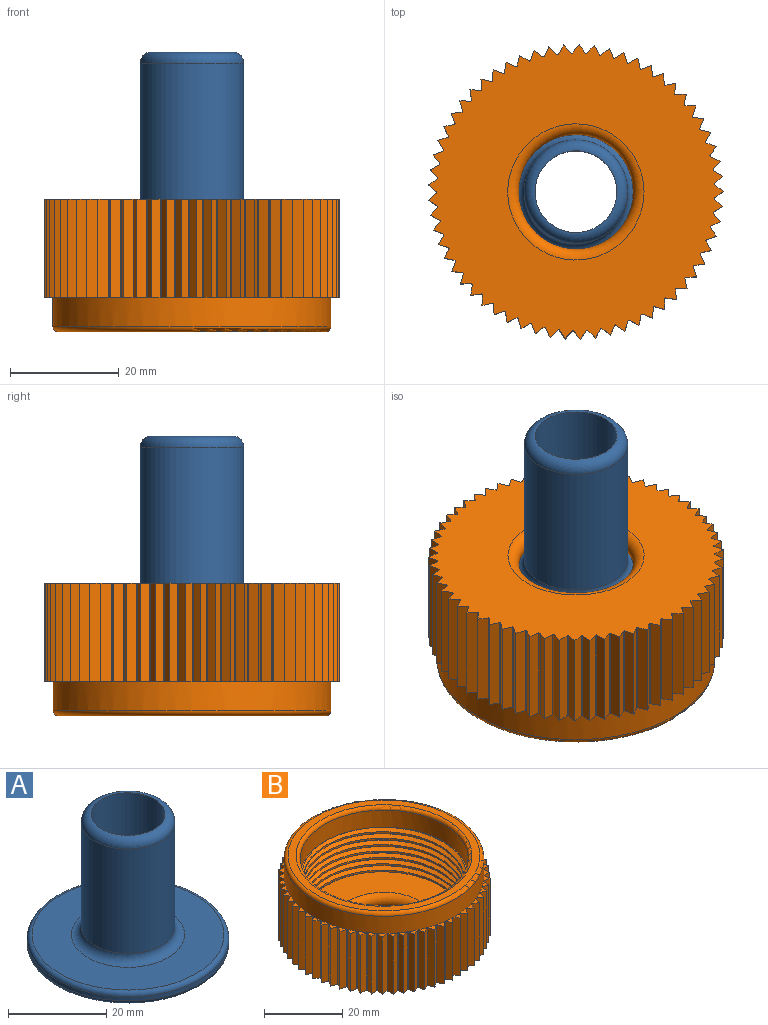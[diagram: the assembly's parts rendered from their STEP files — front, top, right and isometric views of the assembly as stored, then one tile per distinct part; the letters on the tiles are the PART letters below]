
ASSEMBLY  parts=2 mates=1
PART A: 10 faces, bbox 44.4x44.4x33 mm
  f0: cylinder r=20.5mm len=41mm, axis (0,0,-1), area 128.8mm2, adj f7,f8
  f1: cylinder r=7.5mm len=31mm, axis (0,0,-1), area 1460.8mm2, adj f6,f9
  f2: plane 39x39mm, normal (0,0,1), area 779.1mm2, adj f5,f8
  f3: plane 39x39mm, normal (0,0,-1), area 911.1mm2, adj f7,f9
  f4: cylinder r=9.5mm len=26mm, axis (0,0,-1), area 1551.9mm2, adj f5,f6
  f5: torus R=11.5mm, axis (0,0,1), area 201.9mm2, adj f2,f4
  f6: torus R=7.5mm, axis (0,0,1), area 173.2mm2, adj f1,f4
  f7: torus R=19.5mm, axis (0,0,1), area 198.7mm2, adj f0,f3
  f8: torus R=19.5mm, axis (0,0,1), area 198.7mm2, adj f0,f2
  f9: torus R=9.5mm, axis (0,0,1), area 162.4mm2, adj f1,f3
PART B: 197 faces, bbox 56x56x25.1 mm
  f0: plane 2.4x1.71mm, normal (0,0,1), area 1.9mm2, adj f62,f181,f184
  f1: plane 2.37x1.8mm, normal (0,0,1), area 1.9mm2, adj f63,f64,f181
  f2: plane 2.31x1.88mm, normal (0,0,1), area 1.9mm2, adj f65,f66,f181
  f3: plane 2.22x1.94mm, normal (0,0,1), area 1.9mm2, adj f67,f68,f181
  f4: plane 2.11x1.98mm, normal (0,0,1), area 1.9mm2, adj f69,f70,f181
  f5: plane 2x1.98mm, normal (0,0,1), area 1.9mm2, adj f71,f72,f181
  f6: plane 2x1.96mm, normal (0,0,1), area 1.9mm2, adj f73,f74,f181
  f7: plane 1.99x1.97mm, normal (0,0,1), area 1.9mm2, adj f75,f76,f181
  f8: plane 2x1.93mm, normal (0,0,1), area 1.9mm2, adj f77,f78,f181
  f9: plane 2.07x1.99mm, normal (0,0,1), area 1.9mm2, adj f79,f80,f181
  f10: plane 2.18x1.96mm, normal (0,0,1), area 1.9mm2, adj f81,f82,f181
  f11: plane 2.28x1.91mm, normal (0,0,1), area 1.9mm2, adj f83,f84,f181
  f12: plane 2.35x1.83mm, normal (0,0,1), area 1.9mm2, adj f85,f86,f181
  f13: plane 2.4x1.74mm, normal (0,0,1), area 1.9mm2, adj f87,f88,f181
  f14: plane 2.42x1.63mm, normal (0,0,1), area 1.9mm2, adj f89,f90,f181
  f15: plane 2.41x1.68mm, normal (0,0,1), area 1.9mm2, adj f91,f92,f181
  f16: plane 2.38x1.78mm, normal (0,0,1), area 1.9mm2, adj f93,f94,f181
  f17: plane 2.32x1.87mm, normal (0,0,1), area 1.9mm2, adj f95,f96,f181
  f18: plane 2.24x1.93mm, normal (0,0,1), area 1.9mm2, adj f97,f98,f181
  f19: plane 2.14x1.97mm, normal (0,0,1), area 1.9mm2, adj f99,f100,f181
  f20: plane 2.01x2mm, normal (0,0,1), area 1.9mm2, adj f101,f102,f181
  f21: plane 2x1.95mm, normal (0,0,1), area 1.9mm2, adj f103,f104,f181
  f22: plane 1.98x1.98mm, normal (0,0,1), area 1.9mm2, adj f105,f106,f181
  f23: plane 2x1.94mm, normal (0,0,1), area 1.9mm2, adj f107,f108,f181
  f24: plane 2.03x1.99mm, normal (0,0,1), area 1.9mm2, adj f109,f110,f181
  f25: plane 2.16x1.97mm, normal (0,0,1), area 1.9mm2, adj f111,f112,f181
  f26: plane 2.26x1.92mm, normal (0,0,1), area 1.9mm2, adj f113,f114,f181
  f27: plane 2.33x1.85mm, normal (0,0,1), area 1.9mm2, adj f115,f116,f181
  f28: plane 2.39x1.76mm, normal (0,0,1), area 1.9mm2, adj f117,f118,f181
  f29: plane 2.41x1.66mm, normal (0,0,1), area 1.9mm2, adj f119,f120,f181
  f30: plane 2.41x1.65mm, normal (0,0,1), area 1.9mm2, adj f121,f122,f181
  f31: plane 2.39x1.76mm, normal (0,0,1), area 1.9mm2, adj f123,f124,f181
  f32: plane 2.34x1.85mm, normal (0,0,1), area 1.9mm2, adj f125,f126,f181
  f33: plane 2.26x1.92mm, normal (0,0,1), area 1.9mm2, adj f127,f128,f181
  f34: plane 2.17x1.96mm, normal (0,0,1), area 1.9mm2, adj f129,f130,f181
  f35: plane 2.04x1.99mm, normal (0,0,1), area 1.9mm2, adj f131,f132,f181
  f36: plane 2x1.93mm, normal (0,0,1), area 1.9mm2, adj f133,f134,f181
  f37: plane 1.99x1.98mm, normal (0,0,1), area 1.9mm2, adj f135,f136,f181
  f38: plane 2x1.95mm, normal (0,0,1), area 1.9mm2, adj f137,f138,f181
  f39: plane 2x2mm, normal (0,0,1), area 1.9mm2, adj f139,f140,f181
  f40: plane 2.13x1.98mm, normal (0,0,1), area 1.9mm2, adj f141,f142,f181
  f41: plane 2.23x1.93mm, normal (0,0,1), area 1.9mm2, adj f143,f144,f181
  f42: plane 2.32x1.87mm, normal (0,0,1), area 1.9mm2, adj f145,f146,f181
  f43: plane 2.38x1.79mm, normal (0,0,1), area 1.9mm2, adj f147,f148,f181
  f44: plane 2.41x1.69mm, normal (0,0,1), area 1.9mm2, adj f149,f150,f181
  f45: plane 2.42x1.62mm, normal (0,0,1), area 1.9mm2, adj f151,f152,f181
  f46: plane 2.4x1.73mm, normal (0,0,1), area 1.9mm2, adj f153,f154,f181
  f47: plane 2.35x1.83mm, normal (0,0,1), area 1.9mm2, adj f155,f156,f181
  f48: plane 2.29x1.9mm, normal (0,0,1), area 1.9mm2, adj f157,f158,f181
  f49: plane 2.19x1.95mm, normal (0,0,1), area 1.9mm2, adj f159,f160,f181
  f50: plane 2.08x1.99mm, normal (0,0,1), area 1.9mm2, adj f161,f162,f181
  f51: plane 2x1.94mm, normal (0,0,1), area 1.9mm2, adj f163,f164,f181
  f52: plane 1.99x1.97mm, normal (0,0,1), area 1.9mm2, adj f165,f166,f181
  f53: plane 1.99x1.96mm, normal (0,0,1), area 1.9mm2, adj f167,f168,f181
  f54: plane 2x1.96mm, normal (0,0,1), area 1.9mm2, adj f169,f170,f181
  f55: plane 2.1x1.98mm, normal (0,0,1), area 1.9mm2, adj f171,f172,f181
  f56: plane 2.21x1.95mm, normal (0,0,1), area 1.9mm2, adj f173,f174,f181
  f57: plane 2.3x1.89mm, normal (0,0,1), area 1.9mm2, adj f175,f176,f181
  f58: plane 2.36x1.81mm, normal (0,0,1), area 1.9mm2, adj f177,f178,f181
  f59: plane 2.4x1.71mm, normal (0,0,1), area 1.9mm2, adj f179,f180,f181
  f60: plane 2.42x1.6mm, normal (0,0,1), area 1.9mm2, adj f181,f182,f183
  f61: plane 42.7x42.7mm, normal (0,0,1), area 892.4mm2, adj f187,f188,f189,f190,f194
  f62: plane 18x1.71mm, normal (0.52,0.85,0), area 36mm2, adj f0,f181,f184,f185
  f63: plane 18x1.5mm, normal (0.75,-0.66,0), area 36mm2, adj f1,f64,f181,f185
  f64: plane 18x1.8mm, normal (0.43,0.9,0), area 36mm2, adj f1,f63,f181,f185
  f65: plane 18x1.63mm, normal (0.82,-0.58,0), area 36mm2, adj f2,f66,f181,f185
  f66: plane 18x1.88mm, normal (0.34,0.94,0), area 36mm2, adj f2,f65,f181,f185
  f67: plane 18x1.74mm, normal (0.87,-0.49,0), area 36mm2, adj f3,f68,f181,f185
  f68: plane 18x1.94mm, normal (0.24,0.97,0), area 36mm2, adj f3,f67,f181,f185
  f69: plane 18x1.83mm, normal (0.92,-0.4,0), area 36mm2, adj f4,f70,f181,f185
  f70: plane 18x1.98mm, normal (0.14,0.99,0), area 36mm2, adj f4,f69,f181,f185
  f71: plane 18x1.91mm, normal (0.95,-0.3,0), area 36mm2, adj f5,f72,f181,f185
  f72: plane 18x2mm, normal (0.03,1,0), area 36mm2, adj f5,f71,f181,f185
  f73: plane 18x1.96mm, normal (0.98,-0.2,0), area 36mm2, adj f6,f74,f181,f185
  f74: plane 18x2mm, normal (-0.07,1,0), area 36mm2, adj f6,f73,f181,f185
  f75: plane 18x1.99mm, normal (0.99,-0.1,0), area 36mm2, adj f7,f76,f181,f185
  f76: plane 18x1.97mm, normal (-0.17,0.99,0), area 36mm2, adj f7,f75,f181,f185
  f77: plane 18x2mm, normal (1,0,0), area 36mm2, adj f8,f78,f181,f185
  f78: plane 18x1.93mm, normal (-0.27,0.96,0), area 36mm2, adj f8,f77,f181,f185
  f79: plane 18x1.99mm, normal (0.99,0.1,0), area 36mm2, adj f9,f80,f181,f185
  f80: plane 18x1.86mm, normal (-0.37,0.93,0), area 36mm2, adj f9,f79,f181,f185
  f81: plane 18x1.96mm, normal (0.98,0.21,0), area 36mm2, adj f10,f82,f181,f185
  f82: plane 18x1.77mm, normal (-0.46,0.89,0), area 36mm2, adj f10,f81,f181,f185
  f83: plane 18x1.91mm, normal (0.95,0.3,0), area 36mm2, adj f11,f84,f181,f185
  f84: plane 18x1.67mm, normal (-0.55,0.83,0), area 36mm2, adj f11,f83,f181,f185
  f85: plane 18x1.83mm, normal (0.92,0.4,0), area 36mm2, adj f12,f86,f181,f185
  f86: plane 18x1.55mm, normal (-0.63,0.77,0), area 36mm2, adj f12,f85,f181,f185
  f87: plane 18x1.74mm, normal (0.87,0.49,0), area 36mm2, adj f13,f88,f181,f185
  f88: plane 18x1.42mm, normal (-0.71,0.7,0), area 36mm2, adj f13,f87,f181,f185
  f89: plane 18x1.63mm, normal (0.81,0.58,0), area 36mm2, adj f14,f90,f181,f185
  f90: plane 18x1.56mm, normal (-0.78,0.63,0), area 36mm2, adj f14,f89,f181,f185
  f91: plane 18x1.5mm, normal (0.75,0.66,0), area 36mm2, adj f15,f92,f181,f185
  f92: plane 18x1.68mm, normal (-0.84,0.54,0), area 36mm2, adj f15,f91,f181,f185
  f93: plane 18x1.47mm, normal (0.68,0.73,0), area 36mm2, adj f16,f94,f181,f185
  f94: plane 18x1.78mm, normal (-0.89,0.46,0), area 36mm2, adj f16,f93,f181,f185
  f95: plane 18x1.6mm, normal (0.6,0.8,0), area 36mm2, adj f17,f96,f181,f185
  f96: plane 18x1.87mm, normal (-0.93,0.36,0), area 36mm2, adj f17,f95,f181,f185
  f97: plane 18x1.72mm, normal (0.51,0.86,0), area 36mm2, adj f18,f98,f181,f185
  f98: plane 18x1.93mm, normal (-0.96,0.26,0), area 36mm2, adj f18,f97,f181,f185
  f99: plane 18x1.81mm, normal (0.42,0.91,0), area 36mm2, adj f19,f100,f181,f185
  f100: plane 18x1.97mm, normal (-0.99,0.16,0), area 36mm2, adj f19,f99,f181,f185
  f101: plane 18x1.89mm, normal (0.33,0.94,0), area 36mm2, adj f20,f102,f181,f185
  f102: plane 18x2mm, normal (-1,0.06,0), area 36mm2, adj f20,f101,f181,f185
  f103: plane 18x1.95mm, normal (0.23,0.97,0), area 36mm2, adj f21,f104,f181,f185
  f104: plane 18x2mm, normal (-1,-0.04,0), area 36mm2, adj f21,f103,f181,f185
  f105: plane 18x1.98mm, normal (0.13,0.99,0), area 36mm2, adj f22,f106,f181,f185
  f106: plane 18x1.98mm, normal (-0.99,-0.15,0), area 36mm2, adj f22,f105,f181,f185
  f107: plane 18x2mm, normal (0.02,1,0), area 36mm2, adj f23,f108,f181,f185
  f108: plane 18x1.94mm, normal (-0.97,-0.25,0), area 36mm2, adj f23,f107,f181,f185
  f109: plane 18x1.99mm, normal (-0.08,1,0), area 36mm2, adj f24,f110,f181,f185
  f110: plane 18x1.88mm, normal (-0.94,-0.34,0), area 36mm2, adj f24,f109,f181,f185
  f111: plane 18x1.97mm, normal (-0.18,0.98,0), area 36mm2, adj f25,f112,f181,f185
  f112: plane 18x1.8mm, normal (-0.9,-0.44,0), area 36mm2, adj f25,f111,f181,f185
  f113: plane 18x1.92mm, normal (-0.28,0.96,0), area 36mm2, adj f26,f114,f181,f185
  f114: plane 18x1.7mm, normal (-0.85,-0.53,0), area 36mm2, adj f26,f113,f181,f185
  f115: plane 18x1.85mm, normal (-0.38,0.93,0), area 36mm2, adj f27,f116,f181,f185
  f116: plane 18x1.58mm, normal (-0.79,-0.61,0), area 36mm2, adj f27,f115,f181,f185
  f117: plane 18x1.76mm, normal (-0.47,0.88,0), area 36mm2, adj f28,f118,f181,f185
  f118: plane 18x1.44mm, normal (-0.72,-0.69,0), area 36mm2, adj f28,f117,f181,f185
  f119: plane 18x1.66mm, normal (-0.56,0.83,0), area 36mm2, adj f29,f120,f181,f185
  f120: plane 18x1.52mm, normal (-0.65,-0.76,0), area 36mm2, adj f29,f119,f181,f185
  f121: plane 18x1.53mm, normal (-0.64,0.77,0), area 36mm2, adj f30,f122,f181,f185
  f122: plane 18x1.65mm, normal (-0.57,-0.82,0), area 36mm2, adj f30,f121,f181,f185
  f123: plane 18x1.43mm, normal (-0.72,0.7,0), area 36mm2, adj f31,f124,f181,f185
  f124: plane 18x1.76mm, normal (-0.48,-0.88,0), area 36mm2, adj f31,f123,f181,f185
  f125: plane 18x1.57mm, normal (-0.78,0.62,0), area 36mm2, adj f32,f126,f181,f185
  f126: plane 18x1.85mm, normal (-0.39,-0.92,0), area 36mm2, adj f32,f125,f181,f185
  f127: plane 18x1.69mm, normal (-0.84,0.54,0), area 36mm2, adj f33,f128,f181,f185
  f128: plane 18x1.92mm, normal (-0.29,-0.96,0), area 36mm2, adj f33,f127,f181,f185
  f129: plane 18x1.79mm, normal (-0.89,0.45,0), area 36mm2, adj f34,f130,f181,f185
  f130: plane 18x1.96mm, normal (-0.19,-0.98,0), area 36mm2, adj f34,f129,f181,f185
  f131: plane 18x1.87mm, normal (-0.94,0.35,0), area 36mm2, adj f35,f132,f181,f185
  f132: plane 18x1.99mm, normal (-0.09,-1,0), area 36mm2, adj f35,f131,f181,f185
  f133: plane 18x1.93mm, normal (-0.97,0.25,0), area 36mm2, adj f36,f134,f181,f185
  f134: plane 18x2mm, normal (0.02,-1,0), area 36mm2, adj f36,f133,f181,f185
  f135: plane 18x1.98mm, normal (-0.99,0.15,0), area 36mm2, adj f37,f136,f181,f185
  f136: plane 18x1.99mm, normal (0.12,-0.99,0), area 36mm2, adj f37,f135,f181,f185
  f137: plane 18x2mm, normal (-1,0.05,0), area 36mm2, adj f38,f138,f181,f185
  f138: plane 18x1.95mm, normal (0.22,-0.98,0), area 36mm2, adj f38,f137,f181,f185
  f139: plane 18x2mm, normal (-1,-0.05,0), area 36mm2, adj f39,f140,f181,f185
  f140: plane 18x1.89mm, normal (0.32,-0.95,0), area 36mm2, adj f39,f139,f181,f185
  f141: plane 18x1.98mm, normal (-0.99,-0.15,0), area 36mm2, adj f40,f142,f181,f185
  f142: plane 18x1.82mm, normal (0.42,-0.91,0), area 36mm2, adj f40,f141,f181,f185
  f143: plane 18x1.93mm, normal (-0.97,-0.26,0), area 36mm2, adj f41,f144,f181,f185
  f144: plane 18x1.72mm, normal (0.51,-0.86,0), area 36mm2, adj f41,f143,f181,f185
  f145: plane 18x1.87mm, normal (-0.94,-0.35,0), area 36mm2, adj f42,f146,f181,f185
  f146: plane 18x1.61mm, normal (0.59,-0.81,0), area 36mm2, adj f42,f145,f181,f185
  f147: plane 18x1.79mm, normal (-0.89,-0.45,0), area 36mm2, adj f43,f148,f181,f185
  f148: plane 18x1.48mm, normal (0.67,-0.74,0), area 36mm2, adj f43,f147,f181,f185
  f149: plane 18x1.69mm, normal (-0.84,-0.54,0), area 36mm2, adj f44,f150,f181,f185
  f150: plane 18x1.49mm, normal (0.75,-0.67,0), area 36mm2, adj f44,f149,f181,f185
  f151: plane 18x1.57mm, normal (-0.78,-0.62,0), area 36mm2, adj f45,f152,f181,f185
  f152: plane 18x1.62mm, normal (0.81,-0.59,0), area 36mm2, adj f45,f151,f181,f185
  f153: plane 18x1.43mm, normal (-0.72,-0.7,0), area 36mm2, adj f46,f154,f181,f185
  f154: plane 18x1.73mm, normal (0.87,-0.5,0), area 36mm2, adj f46,f153,f181,f185
  f155: plane 18x1.54mm, normal (-0.64,-0.77,0), area 36mm2, adj f47,f156,f181,f185
  f156: plane 18x1.83mm, normal (0.91,-0.41,0), area 36mm2, adj f47,f155,f181,f185
  f157: plane 18x1.66mm, normal (-0.56,-0.83,0), area 36mm2, adj f48,f158,f181,f185
  f158: plane 18x1.9mm, normal (0.95,-0.31,0), area 36mm2, adj f48,f157,f181,f185
  f159: plane 18x1.77mm, normal (-0.47,-0.88,0), area 36mm2, adj f49,f160,f181,f185
  f160: plane 18x1.95mm, normal (0.98,-0.21,0), area 36mm2, adj f49,f159,f181,f185
  f161: plane 18x1.85mm, normal (-0.38,-0.93,0), area 36mm2, adj f50,f162,f181,f185
  f162: plane 18x1.99mm, normal (0.99,-0.11,0), area 36mm2, adj f50,f161,f181,f185
  f163: plane 18x1.92mm, normal (-0.28,-0.96,0), area 36mm2, adj f51,f164,f181,f185
  f164: plane 18x2mm, normal (1,-0.01,0), area 36mm2, adj f51,f163,f181,f185
  f165: plane 18x1.97mm, normal (-0.18,-0.98,0), area 36mm2, adj f52,f166,f181,f185
  f166: plane 18x1.99mm, normal (1,0.09,0), area 36mm2, adj f52,f165,f181,f185
  f167: plane 18x1.99mm, normal (-0.08,-1,0), area 36mm2, adj f53,f168,f181,f185
  f168: plane 18x1.96mm, normal (0.98,0.2,0), area 36mm2, adj f53,f167,f181,f185
  f169: plane 18x2mm, normal (0.03,-1,0), area 36mm2, adj f54,f170,f181,f185
  f170: plane 18x1.91mm, normal (0.96,0.3,0), area 36mm2, adj f54,f169,f181,f185
  f171: plane 18x1.98mm, normal (0.13,-0.99,0), area 36mm2, adj f55,f172,f181,f185
  f172: plane 18x1.84mm, normal (0.92,0.39,0), area 36mm2, adj f55,f171,f181,f185
  f173: plane 18x1.95mm, normal (0.23,-0.97,0), area 36mm2, adj f56,f174,f181,f185
  f174: plane 18x1.75mm, normal (0.87,0.48,0), area 36mm2, adj f56,f173,f181,f185
  f175: plane 18x1.89mm, normal (0.33,-0.94,0), area 36mm2, adj f57,f176,f181,f185
  f176: plane 18x1.64mm, normal (0.82,0.57,0), area 36mm2, adj f57,f175,f181,f185
  f177: plane 18x1.81mm, normal (0.42,-0.91,0), area 36mm2, adj f58,f178,f181,f185
  f178: plane 18x1.51mm, normal (0.76,0.65,0), area 36mm2, adj f58,f177,f181,f185
  f179: plane 18x1.71mm, normal (0.52,-0.86,0), area 36mm2, adj f59,f180,f181,f185
  f180: plane 18x1.46mm, normal (0.69,0.73,0), area 36mm2, adj f59,f179,f181,f185
  f181: cylinder r=25.5mm len=51mm, axis (0,0,-1), area 1085.4mm2, adj f0,f1,f2,f3,f4,f5,f6,f7
  f182: plane 18x1.6mm, normal (0.6,-0.8,0), area 36mm2, adj f60,f181,f183,f185
  f183: plane 18x1.59mm, normal (0.61,0.79,0), area 36mm2, adj f60,f181,f182,f185
  f184: plane 18x1.47mm, normal (0.68,-0.73,0), area 36mm2, adj f0,f62,f181,f185
  f185: plane 54.11x54.1mm, normal (0,0,-1), area 1666.6mm2, adj f62,f63,f64,f65,f66,f67,f68,f69
  f186: plane 43.57x43.57mm, normal (0,0,1), area 66.4mm2, adj f187,f188,f190,f191
  f187: bspline ~49.84x43.17mm, area 1155.8mm2, adj f61,f186,f189,f190,f193
  f188: bspline ~49.84x43.17mm, area 1158.3mm2, adj f61,f186,f189,f190,f193
  f189: bspline ~50.05x43.35mm, area 275.4mm2, adj f61,f187,f188,f193
  f190: cylinder r=20.5mm len=41mm, axis (0,0,1), area 506.4mm2, adj f61,f186,f187,f188
  f191: cylinder r=21.45mm len=42.91mm, axis (0,0,-1), area 719.9mm2, adj f186,f193,f195
  f192: plane 49x49mm, normal (0,0,1), area 301.7mm2, adj f195,f196
  f193: plane 18.21x17.93mm, normal (0,0,-1), area 3.5mm2, adj f187,f188,f189,f191
  f194: torus R=12.5mm, axis (0,0,1), area 443.2mm2, adj f61,f185
  f195: torus R=22.45mm, axis (0,0,1), area 215.3mm2, adj f191,f192
  f196: torus R=24.5mm, axis (0,0,1), area 248.1mm2, adj f181,f192
PLACE A t=(-0.63,0.63,1)mm
PLACE B rot(axis=(1,0,0),180deg) t=(-0.63,0.63,7)mm
MATE fastened A.f0 <-> B.f181  axis (0,0,1) through (-0.63,0.63,4)mm
